# Revit family: Storage-Beam_Mounted-JNBDLO_Lateral_Hang_On_Cabinet_Open-Teknion-R20151
name_source: partatom
category: Furniture
revit_build: Autodesk Revit Architecture 2015 (Build: 20140323_1530(x64)
units: mm (PartAtom-declared; Revit-internal decimal feet)

## types (4) — shared parameters
Assembly Code = E2020200
Manufacturer = Teknion
Manufacturer Fax = 416.661.4586
Part Number = JNBDLO
Product Line = Cityline
Series = Cityline
Sustainability Data = http://www.teknion.com
URL = www.teknion.com
Unit Weight URL = http://www.teknion.com
Warranty = http://www.teknion.com

## per-type parameters (varying)
| type | Description | Fascia Finish | Fascia Tackboard | Model | No Fascia Panel | Product Documentation Link | Product Page URL |
| Felt Tackboard | Lateral hang-On Cabinet - Open, Felt Tackboard, Angled Freestanding Leg Style, 13" High | Fabric-Teknion-RB11-Carbon | Yes | JNBDLOEA13_ | No |  | http://www.teknion.com |
| Fabric Tackboard | Lateral hang-On Cabinet - Open, Fabric Tackboard, Angled Freestanding Leg Style, 13" High | Fabric - Teknion - B153 - Digi Tweed - Obsidian Tweed | Yes | JNBDLOFA13_ | No |  | http://www.teknion.com |
| Magnetic Glass | Lateral hang-On Cabinet - Open, Magnetic Glass, Angled Freestanding Leg Style, 13" High | Back-painted Glass - K7 - Teknion - Very White | No | JNBDLOMA13_ | No | http://www.teknion.com | https://www.teknion.com |
| No Fascia | Lateral hang-On Cabinet - Open, No Fascia, Angled Freestanding Leg Style, 13" High | Fabric - Teknion - B153 - Digi Tweed - Obsidian Tweed | No | JNBDLONA13_ | Yes |  | http://www.teknion.com |

type visibility flags (boolean, named after types; folded from table):
- Felt Tackboard: Yes: (none)
- Fabric Tackboard: Yes: (none)
- Magnetic Glass: Yes: Magnetic Glass
- No Fascia: Yes: (none)

## geometry (parser evidence)
native form markers: Sweep x2
no freeform markers — native parametric forms only
